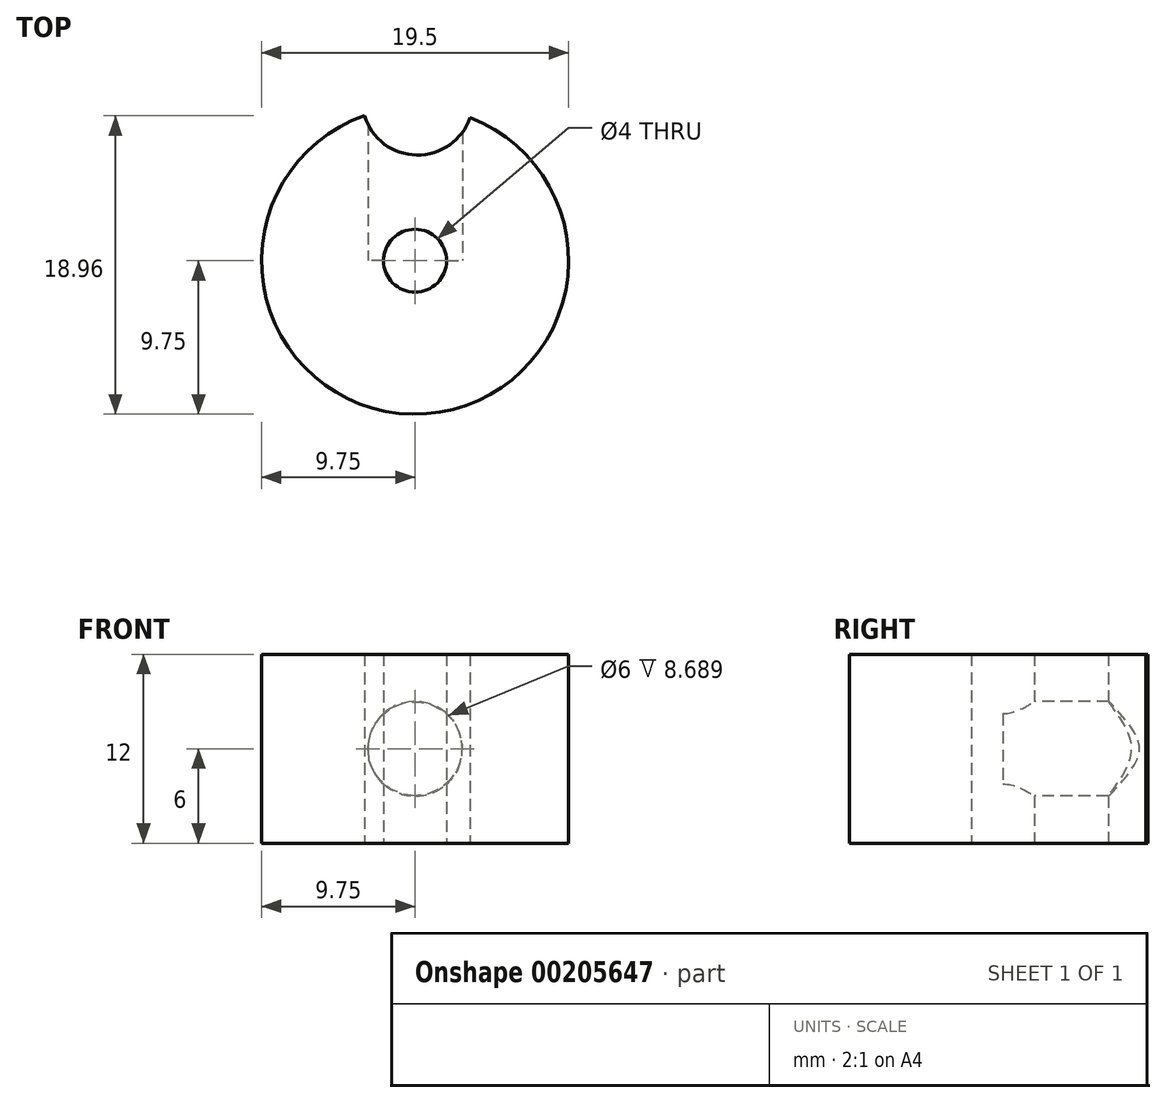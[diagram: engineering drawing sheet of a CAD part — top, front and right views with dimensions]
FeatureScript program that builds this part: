
annotation { "Feature Type Name" : "Feature", "Feature Type Description" : "" }
export const myFeature = defineFeature(function(context is Context, id is Id, definition is map)
    precondition{}
    {
        {
            var Q0;
            Q0=qCreatedBy(makeId("Top.planeOp"),FACE);
            var sketch = newSketch(context, id + "F0", { "sketchPlane" : qUnion([Q0])});
            skCircle(sketch, "E0", {"center": v(0, 0) * mm, "radius": 9.75 * mm});
            skCircle(sketch, "E1", {"center": v(0, 0) * mm, "radius": 2 * mm});
            skArc(sketch, "E2", {"start": v(-3.2, 9.2) * mm, "mid": v(0.1, 6.7) * mm, "end": v(3.49, 9.1) * mm});
            skSolve(sketch);
        }
        {
            var Q0;
            Q0=makeQuery(id+"F0.imprint","IMPRINT",FACE,{"disambiguationData":[TD([[makeQuery(id+"F0.imprint","IMPRINT",EDGE,{"derivedFrom":sQuery(id+"F0.wireOp",EDGE,"E1")}),-1.0]])]});
            extrude(context, id + "F1", {"entities" : qUnion([Q0]), "depth" : 12 * mm});
        }
        {
            var Q0;
            Q0=qCreatedBy(makeId("Front.planeOp"),FACE);
            var sketch = newSketch(context, id + "F2", { "sketchPlane" : qUnion([Q0])});
            skCircle(sketch, "E3", {"center": v(0, 6) * mm, "radius": 3 * mm});
            skSolve(sketch);
        }
        {
            var Q0;
            Q0 = qSketchRegion(id + "F2", true);
            extrude(context, id + "F3", {"entities" : qUnion([Q0]), "operationType" : NewBodyOperationType.REMOVE, "oppositeDirection" : true, "depth" : 25 * mm});
        }
    });
